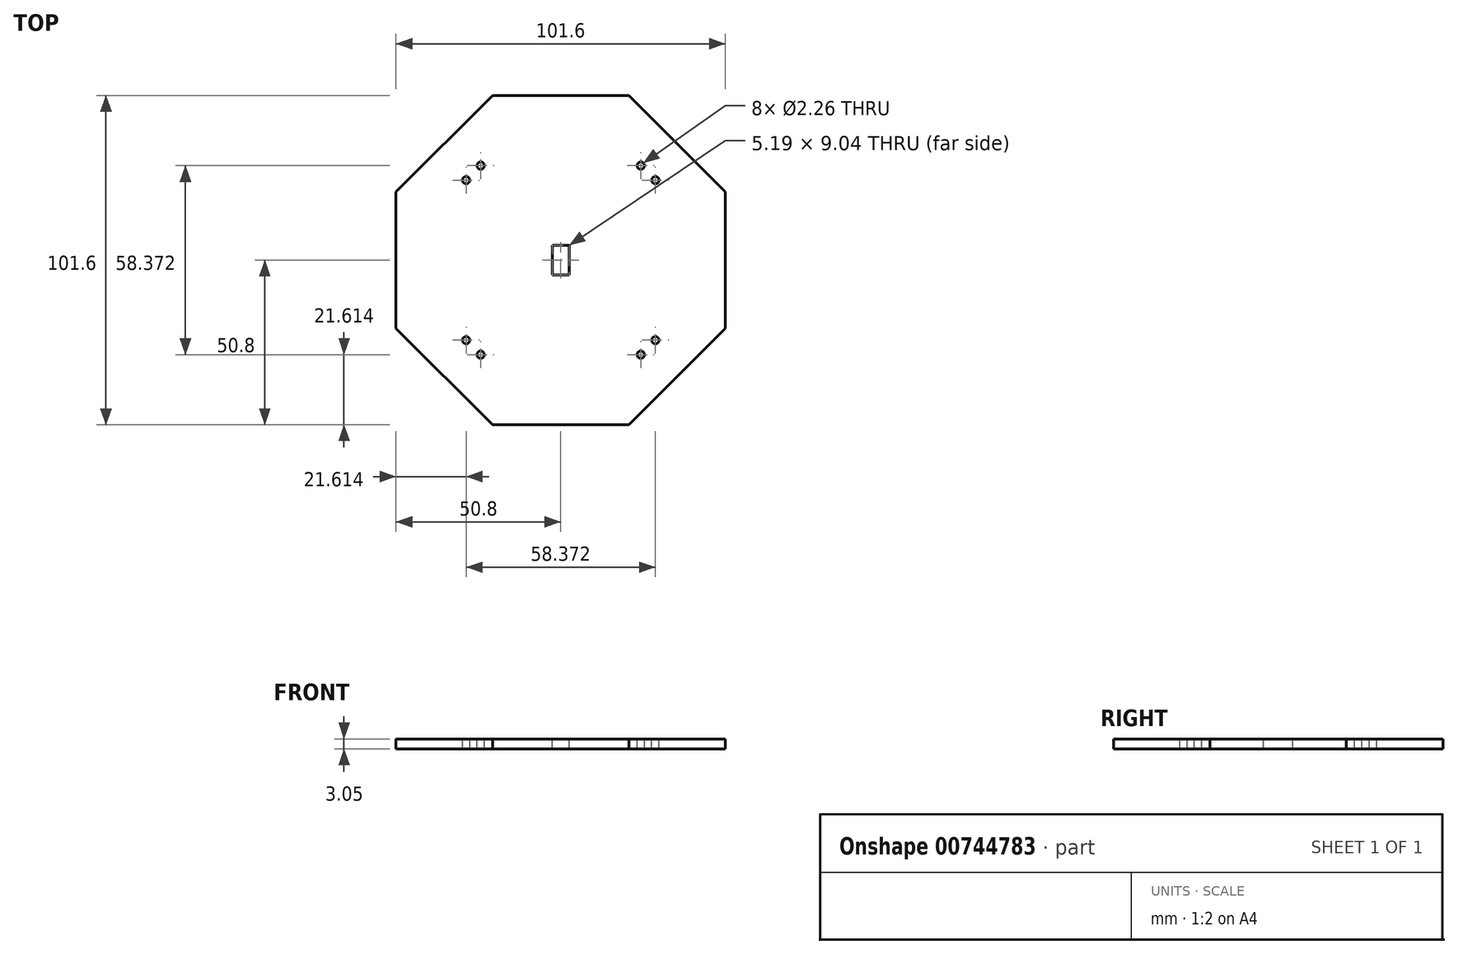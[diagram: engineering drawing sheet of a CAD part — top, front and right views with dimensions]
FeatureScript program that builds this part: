
annotation { "Feature Type Name" : "Feature", "Feature Type Description" : "" }
export const myFeature = defineFeature(function(context is Context, id is Id, definition is map)
    precondition{}
    {
        {
            var Q0;
            Q0=qCreatedBy(makeId("Top.planeOp"),FACE);
            var sketch = newSketch(context, id + "F0", { "sketchPlane" : qUnion([Q0])});
            skCircle(sketch, "E0.cCircle", {"center": v(0, 0) * mm, "radius": 50.8 * mm, "construction": true});
            skLineSegment(sketch, "E0.0", {"start": v(-21.04, 50.8) * mm, "end": v(21.04, 50.8) * mm});
            skLineSegment(sketch, "E0.1", {"start": v(21.04, 50.8) * mm, "end": v(50.8, 21.04) * mm});
            skLineSegment(sketch, "E0.2", {"start": v(50.8, 21.04) * mm, "end": v(50.8, -21.04) * mm});
            skLineSegment(sketch, "E0.3", {"start": v(50.8, -21.04) * mm, "end": v(21.04, -50.8) * mm});
            skLineSegment(sketch, "E0.4", {"start": v(21.04, -50.8) * mm, "end": v(-21.04, -50.8) * mm});
            skLineSegment(sketch, "E0.5", {"start": v(-21.04, -50.8) * mm, "end": v(-50.8, -21.04) * mm});
            skLineSegment(sketch, "E0.6", {"start": v(-50.8, -21.04) * mm, "end": v(-50.8, 21.04) * mm});
            skLineSegment(sketch, "E0.7", {"start": v(-50.8, 21.04) * mm, "end": v(-21.04, 50.8) * mm});
            skPoint(sketch, "E0.0.midPoint", {"position": v(0, 50.8) * mm});
            skSolve(sketch);
        }
        {
            var Q0;
            Q0=makeQuery(id+"F0.imprint","IMPRINT",FACE,{"disambiguationData":[TD([[makeQuery(id+"F0.imprint","IMPRINT",EDGE,{"derivedFrom":sQuery(id+"F0.wireOp",EDGE,"E0.0")}),-1.0]])]});
            extrude(context, id + "F1", {"entities" : qUnion([Q0]), "depth" : 3.05 * mm, "offsetDistance" : 25.4 * mm});
        }
        {
            var Q0;
            Q0=makeQuery(id+"F1.opExtrude","CAP_FACE",FACE,{"disambiguationData":[OSD([sQuery(id+"F0.wireOp",EDGE,"E0.0"),sQuery(id+"F0.wireOp",EDGE,"E0.1"),sQuery(id+"F0.wireOp",EDGE,"E0.2"),sQuery(id+"F0.wireOp",EDGE,"E0.3"),sQuery(id+"F0.wireOp",EDGE,"E0.4"),sQuery(id+"F0.wireOp",EDGE,"E0.5"),sQuery(id+"F0.wireOp",EDGE,"E0.6"),sQuery(id+"F0.wireOp",EDGE,"E0.7")])],"isStart":false});
            var sketch = newSketch(context, id + "F2", { "sketchPlane" : qUnion([Q0])});
            skLineSegment(sketch, "E1", {"start": v(38.17, -33.68) * mm, "end": v(33.68, -38.17) * mm, "construction": true});
            skLineSegment(sketch, "E2", {"start": v(33.68, -38.17) * mm, "end": v(24.7, -29.19) * mm, "construction": true});
            skLineSegment(sketch, "E3", {"start": v(24.7, -29.19) * mm, "end": v(29.19, -24.7) * mm, "construction": true});
            skLineSegment(sketch, "E4", {"start": v(29.19, -24.7) * mm, "end": v(38.17, -33.68) * mm, "construction": true});
            skPoint(sketch, "E5", {"position": v(24.7, -29.19) * mm});
            skPoint(sketch, "E6", {"position": v(29.19, -24.7) * mm});
            skPoint(sketch, "E7", {"position": v(38.17, -33.68) * mm});
            skPoint(sketch, "E8", {"position": v(33.68, -38.17) * mm});
            skLineSegment(sketch, "E9.MirrorCS", {"start": v(-33.68, -38.17) * mm, "end": v(-24.7, -29.19) * mm, "construction": true});
            skLineSegment(sketch, "E10.MirrorCS", {"start": v(-38.17, -33.68) * mm, "end": v(-33.68, -38.17) * mm, "construction": true});
            skLineSegment(sketch, "E11.MirrorCS", {"start": v(-24.7, -29.19) * mm, "end": v(-29.19, -24.7) * mm, "construction": true});
            skLineSegment(sketch, "E12.MirrorCS", {"start": v(-29.19, -24.7) * mm, "end": v(-38.17, -33.68) * mm, "construction": true});
            skPoint(sketch, "E13.MirrorP", {"position": v(-29.19, -24.7) * mm});
            skPoint(sketch, "E14.MirrorP", {"position": v(-24.7, -29.19) * mm});
            skPoint(sketch, "E15.MirrorP", {"position": v(-33.68, -38.17) * mm});
            skPoint(sketch, "E16.MirrorP", {"position": v(-38.17, -33.68) * mm});
            skLineSegment(sketch, "E17.MirrorCS", {"start": v(-24.7, 29.19) * mm, "end": v(-29.19, 24.7) * mm, "construction": true});
            skLineSegment(sketch, "E18.MirrorCS", {"start": v(-38.17, 33.68) * mm, "end": v(-33.68, 38.17) * mm, "construction": true});
            skLineSegment(sketch, "E19.MirrorCS", {"start": v(33.68, 38.17) * mm, "end": v(24.7, 29.19) * mm, "construction": true});
            skLineSegment(sketch, "E20.MirrorCS", {"start": v(38.17, 33.68) * mm, "end": v(33.68, 38.17) * mm, "construction": true});
            skLineSegment(sketch, "E21.MirrorCS", {"start": v(24.7, 29.19) * mm, "end": v(29.19, 24.7) * mm, "construction": true});
            skPoint(sketch, "E22.MirrorP", {"position": v(-38.17, 33.68) * mm});
            skPoint(sketch, "E23.MirrorP", {"position": v(24.7, 29.19) * mm});
            skLineSegment(sketch, "E24.MirrorCS", {"start": v(-29.19, 24.7) * mm, "end": v(-38.17, 33.68) * mm, "construction": true});
            skPoint(sketch, "E25.MirrorP", {"position": v(38.17, 33.68) * mm});
            skPoint(sketch, "E26.MirrorP", {"position": v(33.68, 38.17) * mm});
            skPoint(sketch, "E27.MirrorP", {"position": v(29.19, 24.7) * mm});
            skPoint(sketch, "E28.MirrorP", {"position": v(-24.7, 29.19) * mm});
            skLineSegment(sketch, "E29.MirrorCS", {"start": v(29.19, 24.7) * mm, "end": v(38.17, 33.68) * mm, "construction": true});
            skLineSegment(sketch, "E30.MirrorCS", {"start": v(-33.68, 38.17) * mm, "end": v(-24.7, 29.19) * mm, "construction": true});
            skPoint(sketch, "E31.MirrorP", {"position": v(-33.68, 38.17) * mm});
            skPoint(sketch, "E32.MirrorP", {"position": v(-29.19, 24.7) * mm});
            skSolve(sketch);
        }
        {
            var Q0;
            Q0=sQuery(id+"F2.wireOp",VERTEX,"E28.MirrorP");
            var Q1;
            Q1=sQuery(id+"F2.wireOp",VERTEX,"E32.MirrorP");
            var Q2;
            Q2=sQuery(id+"F2.wireOp",VERTEX,"E13.MirrorP");
            var Q3;
            Q3=sQuery(id+"F2.wireOp",VERTEX,"E14.MirrorP");
            var Q4;
            Q4=sQuery(id+"F2.wireOp",VERTEX,"E5");
            var Q5;
            Q5=sQuery(id+"F2.wireOp",VERTEX,"E6");
            var Q6;
            Q6=sQuery(id+"F2.wireOp",VERTEX,"E27.MirrorP");
            var Q7;
            Q7=sQuery(id+"F2.wireOp",VERTEX,"E23.MirrorP");
            var Q8;
            Q8=makeQuery(id+"F1.opExtrude","SWEPT_BODY",BODY,{"disambiguationData":[OSD([sQuery(id+"F0.wireOp",EDGE,"E0.0"),sQuery(id+"F0.wireOp",EDGE,"E0.1"),sQuery(id+"F0.wireOp",EDGE,"E0.2"),sQuery(id+"F0.wireOp",EDGE,"E0.3"),sQuery(id+"F0.wireOp",EDGE,"E0.4"),sQuery(id+"F0.wireOp",EDGE,"E0.5"),sQuery(id+"F0.wireOp",EDGE,"E0.6"),sQuery(id+"F0.wireOp",EDGE,"E0.7")])]});
            hole(context, id + "F3", {"style" : HoleStyle.SIMPLE, "endStyle" : HoleEndStyle.THROUGH, "standardTappedOrClearance" : lookupTablePath({ "standard" : "ANSI", "fit" : "Close", "size" : "#2", "type" : "Clearance" }), "standardBlindInLast" : lookupTablePath({ "fit" : "Close", "standard" : "ANSI", "size" : "#2", "type" : "Clearance" }), "holeDiameter" : 2.26 * mm, "majorDiameter" : 6.35 * mm, "isTappedThrough" : true, "tappedDepth" : 12.7 * mm, "tapClearance" : 3, "locations" : qUnion([Q0, Q1, Q2, Q3, Q4, Q5, Q6, Q7]), "scope" : qUnion([Q8])});
        }
        {
            var Q0;
            Q0=makeQuery(id+"F1.opExtrude","CAP_FACE",FACE,{"disambiguationData":[OSD([sQuery(id+"F0.wireOp",EDGE,"E0.0"),sQuery(id+"F0.wireOp",EDGE,"E0.1"),sQuery(id+"F0.wireOp",EDGE,"E0.2"),sQuery(id+"F0.wireOp",EDGE,"E0.3"),sQuery(id+"F0.wireOp",EDGE,"E0.4"),sQuery(id+"F0.wireOp",EDGE,"E0.5"),sQuery(id+"F0.wireOp",EDGE,"E0.6"),sQuery(id+"F0.wireOp",EDGE,"E0.7")])],"isStart":false});
            var sketch = newSketch(context, id + "F4", { "sketchPlane" : qUnion([Q0])});
            skLineSegment(sketch, "E33.bottom", {"start": v(2.6, 4.52) * mm, "end": v(-2.6, 4.52) * mm});
            skLineSegment(sketch, "E33.top", {"start": v(2.6, -4.52) * mm, "end": v(-2.6, -4.52) * mm});
            skLineSegment(sketch, "E33.left", {"start": v(2.6, 4.52) * mm, "end": v(2.6, -4.52) * mm});
            skLineSegment(sketch, "E33.right", {"start": v(-2.6, 4.52) * mm, "end": v(-2.6, -4.52) * mm});
            skPoint(sketch, "E33.middle", {"position": v(0, 0) * mm});
            skSolve(sketch);
        }
        {
            var Q0;
            Q0=makeQuery(id+"F4.imprint","IMPRINT",FACE,{"disambiguationData":[TD([[makeQuery(id+"F4.imprint","IMPRINT",EDGE,{"derivedFrom":sQuery(id+"F4.wireOp",EDGE,"E33.bottom")}),1.0]])]});
            extrude(context, id + "F5", {"entities" : qUnion([Q0]), "operationType" : NewBodyOperationType.REMOVE, "oppositeDirection" : true, "depth" : 25.4 * mm, "offsetDistance" : 25.4 * mm});
        }
    });
